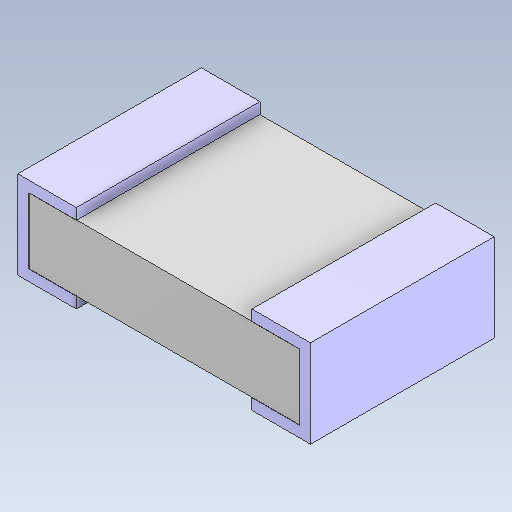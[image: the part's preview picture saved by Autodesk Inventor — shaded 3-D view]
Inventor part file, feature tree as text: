
AUTODESK INVENTOR PART (.ipt)
format: ipt  version: 2020 (Build 240168000, 168)  size: 111,104 bytes
history: native  units: mm
features: other x1, mirror x1
ambient origin geometry x8: Origin, YZ Plane, XZ Plane, XY Plane, X Axis, Y Axis, Z Axis, Center Point
bodies: Body1 (feature_tree)
feature tree (2):
  other  "Твердое тело1"
  mirror  "Mirror1"
